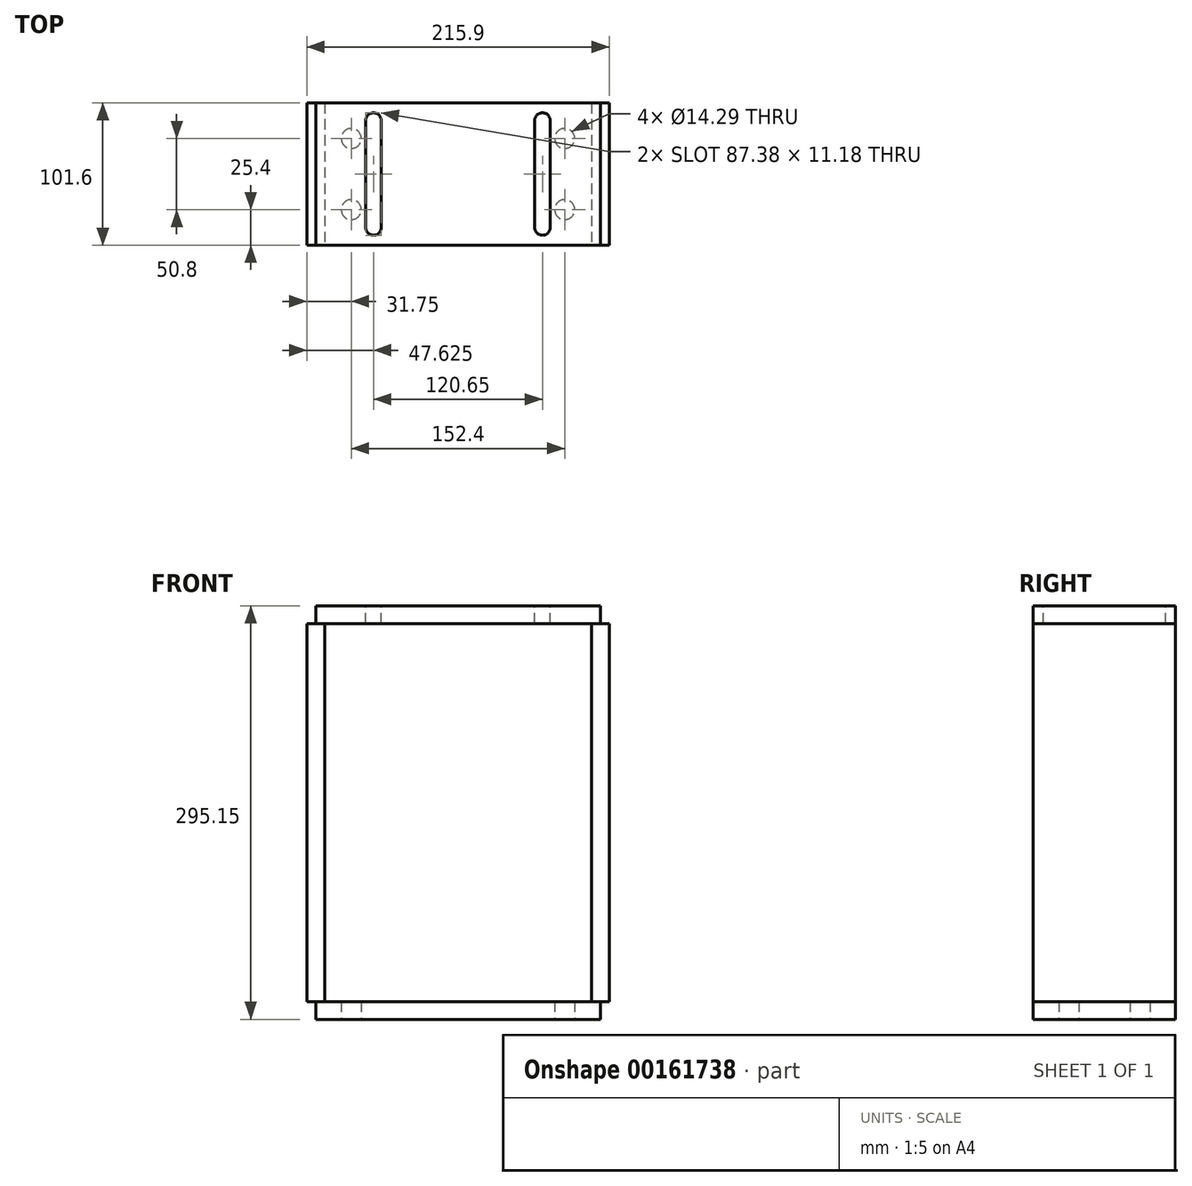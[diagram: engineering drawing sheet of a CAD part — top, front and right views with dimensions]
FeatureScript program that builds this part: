
annotation { "Feature Type Name" : "Feature", "Feature Type Description" : "" }
export const myFeature = defineFeature(function(context is Context, id is Id, definition is map)
    precondition{}
    {
        {
            var Q0;
            Q0=qCreatedBy(makeId("Top.planeOp"),FACE);
            var sketch = newSketch(context, id + "F0", { "sketchPlane" : qUnion([Q0])});
            skLineSegment(sketch, "E0.rect.bottom", {"start": v(-101.6, 50.8) * mm, "end": v(101.6, 50.8) * mm});
            skLineSegment(sketch, "E0.rect.top", {"start": v(-101.6, -50.8) * mm, "end": v(101.6, -50.8) * mm});
            skLineSegment(sketch, "E0.rect.left", {"start": v(-101.6, 50.8) * mm, "end": v(-101.6, -50.8) * mm});
            skLineSegment(sketch, "E0.rect.right", {"start": v(101.6, 50.8) * mm, "end": v(101.6, -50.8) * mm});
            skPoint(sketch, "E0.rect.middle", {"position": v(0, 0) * mm});
            skLineSegment(sketch, "E1", {"start": v(0, 50.8) * mm, "end": v(0, -50.8) * mm, "construction": true});
            skLineSegment(sketch, "E2", {"start": v(-101.6, 0) * mm, "end": v(101.6, 0) * mm, "construction": true});
            skLineSegment(sketch, "E3.0", {"start": v(-76.2, 50.8) * mm, "end": v(-76.2, -50.8) * mm, "construction": true});
            skLineSegment(sketch, "E4.0", {"start": v(-101.6, -25.4) * mm, "end": v(101.6, -25.4) * mm, "construction": true});
            skPoint(sketch, "E5", {"position": v(-76.2, -25.4) * mm});
            skPoint(sketch, "E6.0.1.0", {"position": v(-76.2, 25.4) * mm});
            skPoint(sketch, "E6.1.0.0", {"position": v(76.2, -25.4) * mm});
            skPoint(sketch, "E6.1.1.0", {"position": v(76.2, 25.4) * mm});
            skLineSegment(sketch, "E6.direction1", {"start": v(-76.2, -25.4) * mm, "end": v(76.2, -25.4) * mm, "construction": true});
            skLineSegment(sketch, "E6.direction2", {"start": v(-76.2, -25.4) * mm, "end": v(-76.2, 25.4) * mm, "construction": true});
            skSolve(sketch);
        }
        {
            var Q0;
            Q0=makeQuery(id+"F0.imprint","IMPRINT",FACE,{"disambiguationData":[TD([[makeQuery(id+"F0.imprint","IMPRINT",EDGE,{"derivedFrom":sQuery(id+"F0.wireOp",EDGE,"E0.rect.bottom")}),-1.0]])]});
            extrude(context, id + "F1", {"entities" : qUnion([Q0]), "depth" : 12.7 * mm});
        }
        {
            var Q0;
            Q0=sQuery(id+"F0.wireOp",VERTEX,"E5");
            var Q1;
            Q1=sQuery(id+"F0.wireOp",VERTEX,"E6.0.1.0");
            var Q2;
            Q2=sQuery(id+"F0.wireOp",VERTEX,"E6.1.1.0");
            var Q3;
            Q3=sQuery(id+"F0.wireOp",VERTEX,"E6.1.0.0");
            var Q4;
            Q4=makeQuery(id+"F1.opExtrude","SWEPT_BODY",BODY,{"disambiguationData":[OSD([sQuery(id+"F0.wireOp",EDGE,"E0.rect.bottom"),sQuery(id+"F0.wireOp",EDGE,"E0.rect.top"),sQuery(id+"F0.wireOp",EDGE,"E0.rect.left"),sQuery(id+"F0.wireOp",EDGE,"E0.rect.right")])]});
            hole(context, id + "F2", {"style" : HoleStyle.SIMPLE, "holeDiameter" : 14.29 * mm, "endStyle" : HoleEndStyle.THROUGH, "oppositeDirection" : true, "locations" : qUnion([Q0, Q1, Q2, Q3]), "scope" : qUnion([Q4])});
        }
        {
            var Q0;
            Q0=qCreatedBy(makeId("Top.planeOp"),FACE);
            cPlane(context, id + "F3", {"entities" : qUnion([Q0]), "cplaneType" : CPlaneType.OFFSET, "offset" : 295.15 * mm, "width" : 152.4 * mm, "height" : 152.4 * mm});
        }
        {
            var Q0;
            Q0=qCreatedBy(id+"F3.planeOp",FACE);
            var sketch = newSketch(context, id + "F4", { "sketchPlane" : qUnion([Q0])});
            skLineSegment(sketch, "E7.0", {"start": v(-101.6, 50.8) * mm, "end": v(101.6, 50.8) * mm});
            skLineSegment(sketch, "E8.0", {"start": v(-101.6, 50.8) * mm, "end": v(-101.6, -50.8) * mm});
            skLineSegment(sketch, "E9.0", {"start": v(-101.6, -50.8) * mm, "end": v(101.6, -50.8) * mm});
            skLineSegment(sketch, "E10.0", {"start": v(101.6, 50.8) * mm, "end": v(101.6, -50.8) * mm});
            skLineSegment(sketch, "E11", {"start": v(-101.6, 0) * mm, "end": v(101.6, 0) * mm, "construction": true});
            skLineSegment(sketch, "E12", {"start": v(0, 50.8) * mm, "end": v(0, -50.8) * mm, "construction": true});
            skLineSegment(sketch, "E13.0", {"start": v(-60.32, 38.1) * mm, "end": v(-60.33, -38.1) * mm, "construction": true});
            skLineSegment(sketch, "E14.0", {"start": v(-101.6, 38.1) * mm, "end": v(101.6, 38.1) * mm, "construction": true});
            skLineSegment(sketch, "E15.0", {"start": v(-101.6, -38.1) * mm, "end": v(101.6, -38.1) * mm, "construction": true});
            skArc(sketch, "E16.0.startCap", {"start": v(-65.91, 38.1) * mm, "mid": v(-60.32, 43.69) * mm, "end": v(-54.74, 38.1) * mm});
            skArc(sketch, "E16.0.endCap", {"start": v(-54.74, -38.1) * mm, "mid": v(-60.33, -43.69) * mm, "end": v(-65.91, -38.1) * mm});
            skLineSegment(sketch, "E16.0.left", {"start": v(-54.74, 38.1) * mm, "end": v(-54.74, -38.1) * mm});
            skLineSegment(sketch, "E16.0.right", {"start": v(-65.91, 38.1) * mm, "end": v(-65.91, -38.1) * mm});
            skArc(sketch, "E17.MirrorCS", {"start": v(65.91, 38.1) * mm, "mid": v(60.33, 43.69) * mm, "end": v(54.74, 38.1) * mm});
            skArc(sketch, "E18.MirrorCS", {"start": v(54.74, -38.1) * mm, "mid": v(60.32, -43.69) * mm, "end": v(65.91, -38.1) * mm});
            skLineSegment(sketch, "E19.MirrorCS", {"start": v(65.91, 38.1) * mm, "end": v(65.91, -38.1) * mm});
            skLineSegment(sketch, "E20.MirrorCS", {"start": v(54.74, 38.1) * mm, "end": v(54.74, -38.1) * mm});
            skLineSegment(sketch, "E21.MirrorCS", {"start": v(60.33, 38.1) * mm, "end": v(60.32, -38.1) * mm, "construction": true});
            skSolve(sketch);
        }
        {
            var Q0;
            Q0=qSketchRegion(id+"F4",true);
            extrude(context, id + "F5", {"entities" : qUnion([Q0]), "oppositeDirection" : true, "depth" : 12.7 * mm});
        }
        {
            var Q0;
            Q0=makeQuery(id+"F5.opExtrude","SWEPT_FACE",FACE,{"disambiguationData":[OSD([sQuery(id+"F4.wireOp",EDGE,"E10.0")])]});
            var sketch = newSketch(context, id + "F6", { "sketchPlane" : qUnion([Q0])});
            skLineSegment(sketch, "E22.0", {"start": v(50.8, 282.45) * mm, "end": v(-50.8, 282.45) * mm, "construction": true});
            skLineSegment(sketch, "E23.0", {"start": v(50.8, 12.7) * mm, "end": v(-50.8, 12.7) * mm, "construction": true});
            skLineSegment(sketch, "E24.bottom", {"start": v(-50.8, 282.45) * mm, "end": v(50.8, 282.45) * mm});
            skLineSegment(sketch, "E24.top", {"start": v(-50.8, 12.7) * mm, "end": v(50.8, 12.7) * mm});
            skLineSegment(sketch, "E24.left", {"start": v(-50.8, 282.45) * mm, "end": v(-50.8, 12.7) * mm});
            skLineSegment(sketch, "E24.right", {"start": v(50.8, 282.45) * mm, "end": v(50.8, 12.7) * mm});
            skSolve(sketch);
        }
        {
            var Q0;
            Q0=qSketchRegion(id+"F6",true);
            extrude(context, id + "F7", {"entities" : qUnion([Q0]), "endBound" : BoundingType.SYMMETRIC, "depth" : 12.7 * mm});
        }
        {
            var Q0;
            Q0=makeQuery(id+"F7.opExtrude","SWEPT_BODY",BODY,{"disambiguationData":[OSD([sQuery(id+"F6.wireOp",EDGE,"E24.bottom"),sQuery(id+"F6.wireOp",EDGE,"E24.top"),sQuery(id+"F6.wireOp",EDGE,"E24.left"),sQuery(id+"F6.wireOp",EDGE,"E24.right")])]});
            var Q1;
            Q1=qCreatedBy(makeId("Right.planeOp"),FACE);
            mirror(context, id + "F8", {"entities" : qUnion([Q0]), "mirrorPlane" : qUnion([Q1])});
        }
    });
